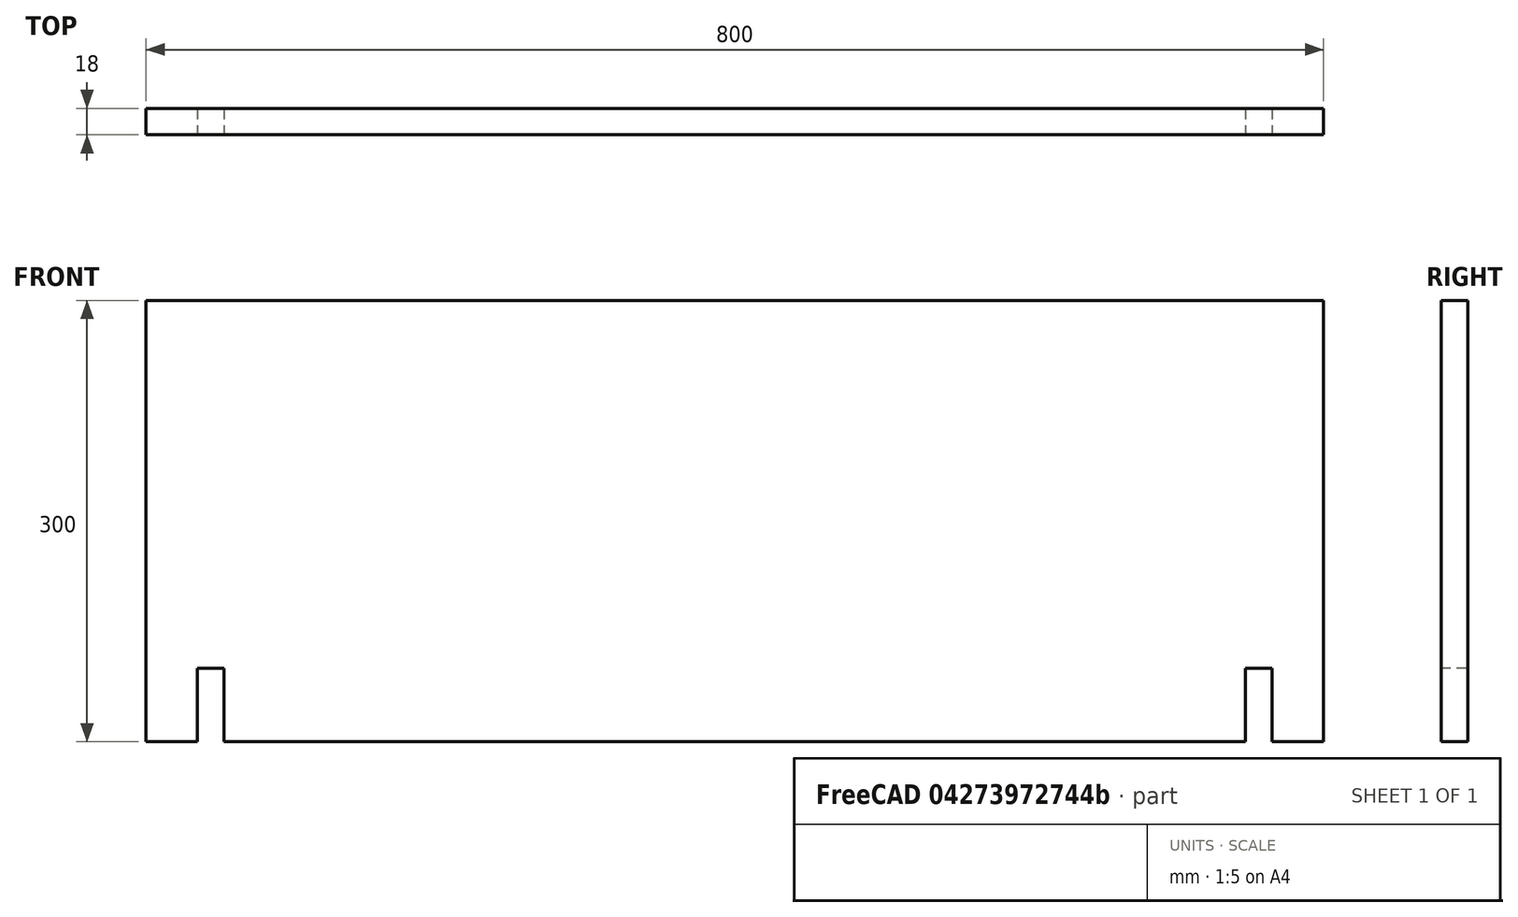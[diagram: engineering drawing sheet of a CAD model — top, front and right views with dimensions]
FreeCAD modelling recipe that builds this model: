
FCSTD DOCUMENT  (FreeCAD 0.19R24267 +148 (Git))
Label: Wood Backplane
License: All rights reserved
LicenseURL: http://en.wikipedia.org/wiki/All_rights_reserved
objects: Sketcher::SketchObject×1, PartDesign::Pad×1, PartDesign::Body×1
note: 4 computed .brp shape members not serialized (recipe doc carries the construction recipe); baked Part::Feature solids carry a one-line shape summary decoded from their .brp

FEATURE [Sketcher::SketchObject] Sketch
  FullyConstrained = true
  MapMode = 5
  Placement = pos=(0,0,0) rot=(1,0,0;1.5708rad)
  Support = -> [XZ_Plane]
  sketch-geometry (18):
    g0: LineSegment StartX=0 StartY=0 StartZ=0 EndX=35 EndY=0 EndZ=0
    g1: LineSegment StartX=800 StartY=0 StartZ=0 EndX=800 EndY=300 EndZ=0
    g2: LineSegment StartX=800 StartY=300 StartZ=0 EndX=0 EndY=300 EndZ=0
    g3: LineSegment StartX=0 StartY=300 StartZ=0 EndX=0 EndY=0 EndZ=0
    g4: LineSegment StartX=53 StartY=0 StartZ=0 EndX=53 EndY=50 EndZ=0
    g5: LineSegment StartX=53 StartY=50 StartZ=0 EndX=35 EndY=50 EndZ=0
    g6: LineSegment StartX=35 StartY=50 StartZ=0 EndX=35 EndY=0 EndZ=0
    g7: LineSegment StartX=765 StartY=0 StartZ=0 EndX=765 EndY=50 EndZ=0
    g8: LineSegment StartX=765 StartY=50 StartZ=0 EndX=747 EndY=50 EndZ=0
    g9: LineSegment StartX=747 StartY=50 StartZ=0 EndX=747 EndY=0 EndZ=0
    g10: LineSegment StartX=53 StartY=0 StartZ=0 EndX=747 EndY=0 EndZ=0
    g11: LineSegment StartX=765 StartY=0 StartZ=0 EndX=800 EndY=0 EndZ=0
    g12: LineSegment StartX=0 StartY=300 StartZ=0 EndX=375 EndY=412.5 EndZ=0
    g13: LineSegment StartX=375 StartY=412.5 StartZ=0 EndX=0 EndY=525 EndZ=0
    g14: LineSegment StartX=0 StartY=525 StartZ=0 EndX=0 EndY=300 EndZ=0
    g15: LineSegment StartX=800 StartY=300 StartZ=0 EndX=800 EndY=525 EndZ=0
    g16: LineSegment StartX=800 StartY=525 StartZ=0 EndX=425 EndY=412.5 EndZ=0
    g17: LineSegment StartX=425 StartY=412.5 StartZ=0 EndX=800 EndY=300 EndZ=0
  constraints (50):
    c: Coincident(g11,g1)
    c: Coincident(g1,g2)
    c: Coincident(g2,g3)
    c: Coincident(g3,g0)
    c: Horizontal(g0)
    c: Horizontal(g2)
    c: Vertical(g1)
    c: Vertical(g3)
    c: Coincident(g0,g-1)
    c: Coincident(g4,g5)
    c: Coincident(g5,g6)
    c: Horizontal(g5)
    c: Vertical(g4)
    c: Vertical(g6)
    c: Coincident(g7,g8)
    c: Coincident(g8,g9)
    c: Horizontal(g8)
    c: Vertical(g7)
    c: Vertical(g9)
    c: PointOnObject(g9,g0)
    c: Tangent(g0,g10)
    c: Tangent(g10,g11)
    c: Equal(g5,g8)
    c: Coincident(g10,g4)
    c: Coincident(g6,g0)
    c: PointOnObject(g10,g9)
    c: Coincident(g11,g7)
    c: Equal(g11,g0)
    c: Equal(g9,g4)
    c: DistanceX(g0,g4) = 18
    c: DistanceX(g10,g10) = 694
    c: DistanceY(g3,g3) = 300
    c: DistanceY(g6,g6) = 50
    c: Coincident(g12,g2)
    c: Coincident(g13,g12)
    c: PointOnObject(g13,g-2)
    c: Coincident(g14,g13)
    c: Coincident(g14,g2)
    c: DistanceX(g13,g12) = 375
    c: Equal(g13,g12)
    c: DistanceY(g14,g14) = 225
    c: Coincident(g15,g1)
    c: Vertical(g15)
    c: Coincident(g16,g15)
    c: Coincident(g17,g16)
    c: Coincident(g17,g1)
    c: Equal(g15,g14)
    c: Equal(g13,g16)
    c: Equal(g17,g16)
    c: DistanceX(g0,g1) = 800
FEATURE [PartDesign::Pad] Pad
  Direction = (1,1,1)
  Length = 18
  Length2 = 100
  Placement = pos=(0,0,0) rot=(1,0,0;1.5708rad)
  Profile = -> Sketch
  Type = 0
FEATURE [PartDesign::Body] Body
  Group = -> [Sketch,Pad]
  Origin = -> Origin
  Tip = -> Pad
